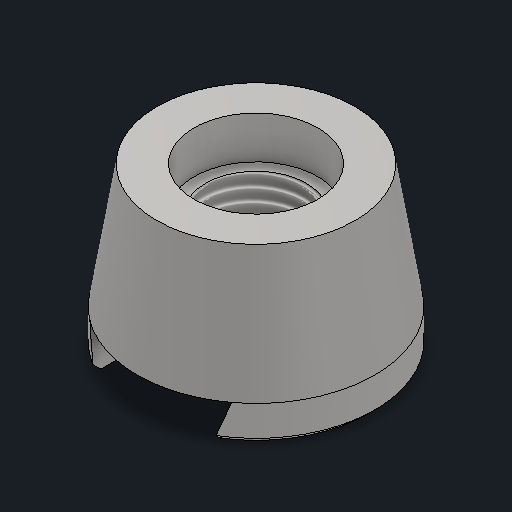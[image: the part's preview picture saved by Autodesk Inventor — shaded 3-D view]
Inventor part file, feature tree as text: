
AUTODESK INVENTOR PART (.ipt)
format: ipt  version: 2025.1 (Build 291241020, 241B)  size: 163,328 bytes
history: native  units: in
note: dims shown in document units (in); Inventor stores cm internally (conversion verified against a paired STEP export)
features: sketch x4, extrude x3, plane x2, other x2, loft x1, hole x1, chamfer x1, projected_geometry x1
ambient origin geometry x8: Origin, YZ Plane, XZ Plane, XY Plane, X Axis, Y Axis, Z Axis, Center Point
bodies: Solid1 (feature_tree)
feature tree (15):
  extrude  "Extrusion1"  Depth=0.06in TaperAngle=0.0deg
  sketch  "Sketch2"  dims[d3=-0.265in d4=0.3275in]
  plane  "Work Plane1"
  sketch  "Sketch3"  dims[d5=0.0in d6=90.0deg d7=0.0in d8=90.0deg]
  loft  "Loft1"
  hole  "Hole1"  [1 undecoded]
  extrude  "Extrusion3"  Depth=0.07in TaperAngle=0.0deg
  plane  "Work Plane2"
  chamfer  "Chamfer1"  Distance=0.1975in
  extrude  "Extrusion4"  Depth=0.235in
  sketch  "Sketch1"  dims[d0=0.393in d1=0.06in d2=0.0in]
  other  "Edges1"
  sketch  "Sketch4"  dims[d9=0.205in d14=0.167in d15=0.38in d16=0.375in d17=0.25in d18=0.5635in d19=0.64in d20=0.8108in d21=0.07in d22=0.0in d23=0.1975in d24=0.235in d25=0.0in d26=0.0in d27=0.01in d28=0.125in d29=45.0deg]
  projected_geometry  "Projected Loop1"
  other  "Finish1"
note: 1 required parameter value undecoded (feature->parameter linkage not recoverable at this tier; creation-order binding heuristic only, values carry confidence <= 0.55)
